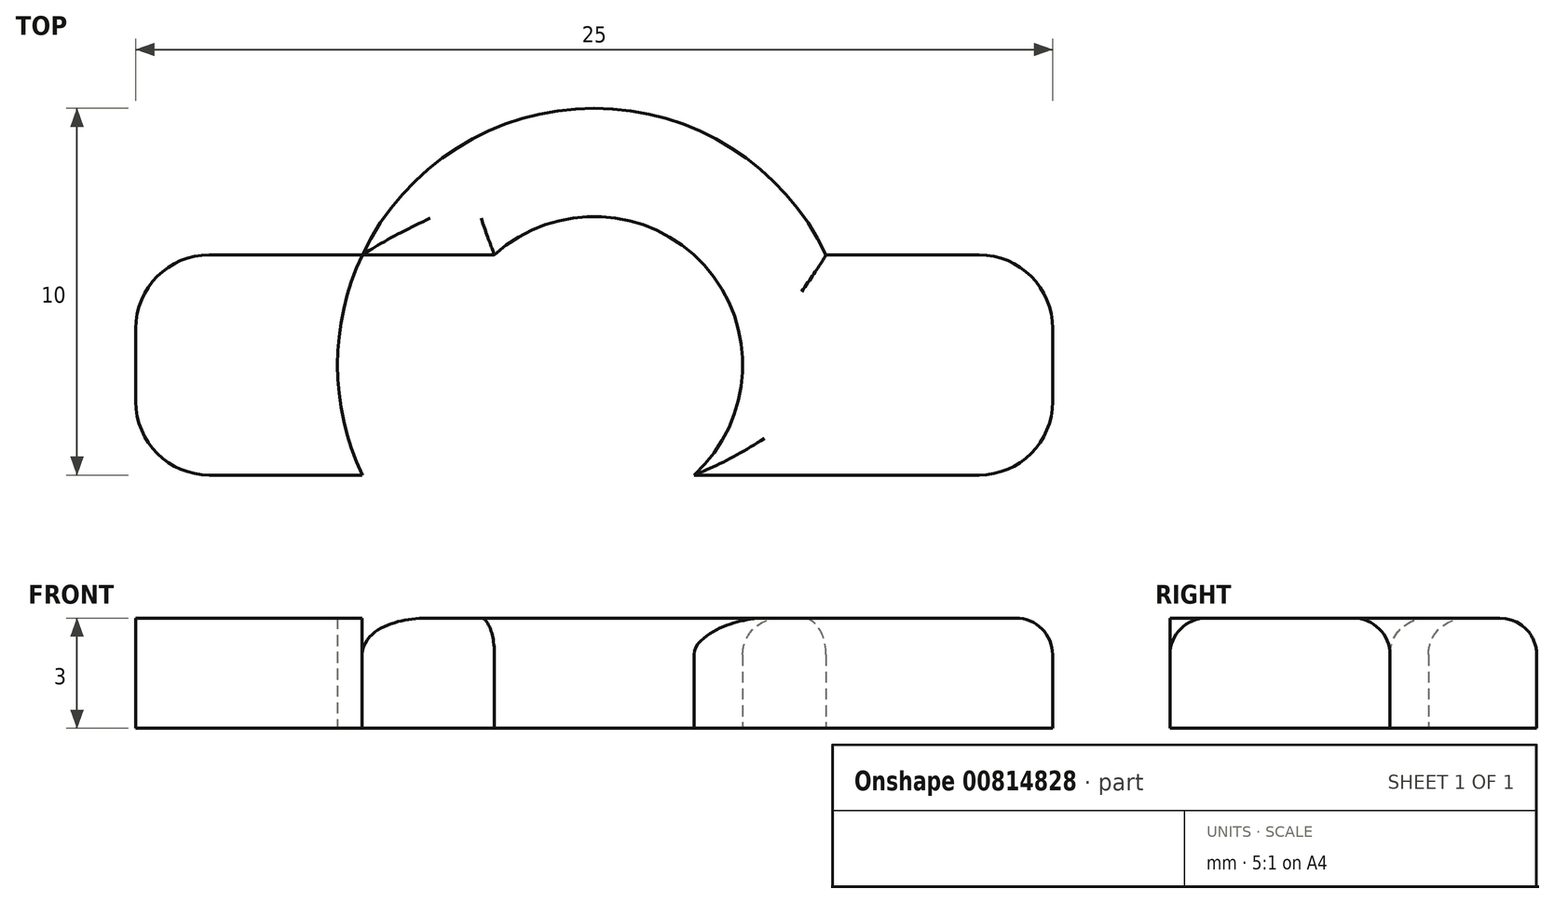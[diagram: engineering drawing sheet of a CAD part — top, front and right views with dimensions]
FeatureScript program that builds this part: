
annotation { "Feature Type Name" : "Feature", "Feature Type Description" : "" }
export const myFeature = defineFeature(function(context is Context, id is Id, definition is map)
    precondition{}
    {
        {
            assignVariable(context, id + "F0", {"name" : "Lenght", "anyValue" : 3});
        }
        {
            var Q0;
            Q0=qCreatedBy(makeId("Top.planeOp"),FACE);
            var sketch = newSketch(context, id + "F1", { "sketchPlane" : qUnion([Q0])});
            skCircle(sketch, "E0", {"center": v(0, 0) * mm, "radius": 4.05 * mm});
            skCircle(sketch, "E1", {"center": v(0, 0) * mm, "radius": 7 * mm});
            skLineSegment(sketch, "E2.bottom", {"start": v(12.5, -3) * mm, "end": v(-12.5, -3) * mm});
            skLineSegment(sketch, "E2.top", {"start": v(12.5, 3) * mm, "end": v(-12.5, 3) * mm});
            skLineSegment(sketch, "E2.left", {"start": v(12.5, -3) * mm, "end": v(12.5, 3) * mm});
            skLineSegment(sketch, "E2.right", {"start": v(-12.5, -3) * mm, "end": v(-12.5, 3) * mm});
            skSolve(sketch);
        }
        {
            var Q0;
            {var subQ5=sQuery(id+"F1.wireOp",EDGE,"E2.right");Q0=makeQuery(id+"F1.imprint","IMPRINT",FACE,{"disambiguationData":[TD([[makeQuery(id+"F1.imprint","IMPRINT",EDGE,{"derivedFrom":subQ5}),-1.0]])]});}
            var Q1;
            {var subQ0=sQuery(id+"F1.wireOp",EDGE,"E2.bottom");var subQ1=sQuery(id+"F1.wireOp",EDGE,"E0");var subQ2=makeQuery(id+"F1.imprint","INTERSECT",VERTEX,{"disambiguationData":[OD(0.0)],"derivedFrom":[subQ1,subQ0]});Q1=makeQuery(id+"F1.imprint","IMPRINT",FACE,{"disambiguationData":[TD([[makeQuery(id+"F1.imprint","IMPRINT",EDGE,{"disambiguationData":[TD([[subQ2,-1.0]])],"derivedFrom":subQ1}),-1.0]])]});}
            var Q2;
            {var subQ0=sQuery(id+"F1.wireOp",EDGE,"E2.top");var subQ1=sQuery(id+"F1.wireOp",EDGE,"E0");var subQ2=makeQuery(id+"F1.imprint","INTERSECT",VERTEX,{"disambiguationData":[OD(0.0)],"derivedFrom":[subQ1,subQ0]});Q2=makeQuery(id+"F1.imprint","IMPRINT",FACE,{"disambiguationData":[TD([[makeQuery(id+"F1.imprint","IMPRINT",EDGE,{"disambiguationData":[TD([[subQ2,-1.0]])],"derivedFrom":subQ1}),-1.0]])]});}
            var Q3;
            {var subQ0=sQuery(id+"F1.wireOp",EDGE,"E2.top");var subQ1=sQuery(id+"F1.wireOp",EDGE,"E0");var subQ2=makeQuery(id+"F1.imprint","INTERSECT",VERTEX,{"disambiguationData":[OD(0.0)],"derivedFrom":[subQ1,subQ0]});Q3=makeQuery(id+"F1.imprint","IMPRINT",FACE,{"disambiguationData":[TD([[makeQuery(id+"F1.imprint","IMPRINT",EDGE,{"disambiguationData":[TD([[subQ2,1.0]])],"derivedFrom":subQ1}),-1.0]])]});}
            var Q4;
            {var subQ0=sQuery(id+"F1.wireOp",EDGE,"E2.top");var subQ1=sQuery(id+"F1.wireOp",EDGE,"E0");var subQ2=makeQuery(id+"F1.imprint","INTERSECT",VERTEX,{"disambiguationData":[OD(1.0)],"derivedFrom":[subQ1,subQ0]});Q4=makeQuery(id+"F1.imprint","IMPRINT",FACE,{"disambiguationData":[TD([[makeQuery(id+"F1.imprint","IMPRINT",EDGE,{"disambiguationData":[TD([[subQ2,1.0]])],"derivedFrom":subQ1}),-1.0]])]});}
            var Q5;
            {var subQ5=sQuery(id+"F1.wireOp",EDGE,"E2.left");Q5=makeQuery(id+"F1.imprint","IMPRINT",FACE,{"disambiguationData":[TD([[makeQuery(id+"F1.imprint","IMPRINT",EDGE,{"derivedFrom":subQ5}),1.0]])]});}
            extrude(context, id + "F2", {"entities" : qUnion([Q0, Q1, Q2, Q3, Q4, Q5]), "depth" : (getVariable(context, 'Lenght')) * mm, "offsetDistance" : 25 * mm});
        }
        {
            var Q0;
            Q0=makeQuery(id+"F2.opExtrude","SWEPT_EDGE",EDGE,{"disambiguationData":[OSD([sQuery(id+"F1.wireOp",EDGE,"E2.bottom"),sQuery(id+"F1.wireOp",EDGE,"E2.right")])]});
            var Q1;
            Q1=makeQuery(id+"F2.opExtrude","SWEPT_EDGE",EDGE,{"disambiguationData":[OSD([sQuery(id+"F1.wireOp",EDGE,"E2.top"),sQuery(id+"F1.wireOp",EDGE,"E2.right")])]});
            var Q2;
            Q2=makeQuery(id+"F2.opExtrude","SWEPT_EDGE",EDGE,{"disambiguationData":[OSD([sQuery(id+"F1.wireOp",EDGE,"E2.bottom"),sQuery(id+"F1.wireOp",EDGE,"E2.left")])]});
            var Q3;
            Q3=makeQuery(id+"F2.opExtrude","SWEPT_EDGE",EDGE,{"disambiguationData":[OSD([sQuery(id+"F1.wireOp",EDGE,"E2.top"),sQuery(id+"F1.wireOp",EDGE,"E2.left")])]});
            fillet(context, id + "F3", {"entities" : qUnion([Q0, Q1, Q2, Q3]), "radius" : 2 * mm, "tangentPropagation" : true, "allowEdgeOverflow" : false});
        }
        {
            var Q0;
            Q0=makeQuery(id+"F2.opExtrude","CAP_FACE",FACE,{"disambiguationData":[OSD([sQuery(id+"F1.wireOp",EDGE,"E0"),sQuery(id+"F1.wireOp",EDGE,"E1"),sQuery(id+"F1.wireOp",EDGE,"E2.bottom"),sQuery(id+"F1.wireOp",EDGE,"E2.top"),sQuery(id+"F1.wireOp",EDGE,"E2.left"),sQuery(id+"F1.wireOp",EDGE,"E2.right")])],"isStart":false});
            fillet(context, id + "F4", {"entities" : qUnion([Q0]), "radius" : 1 * mm, "tangentPropagation" : true, "allowEdgeOverflow" : false});
        }
    });
